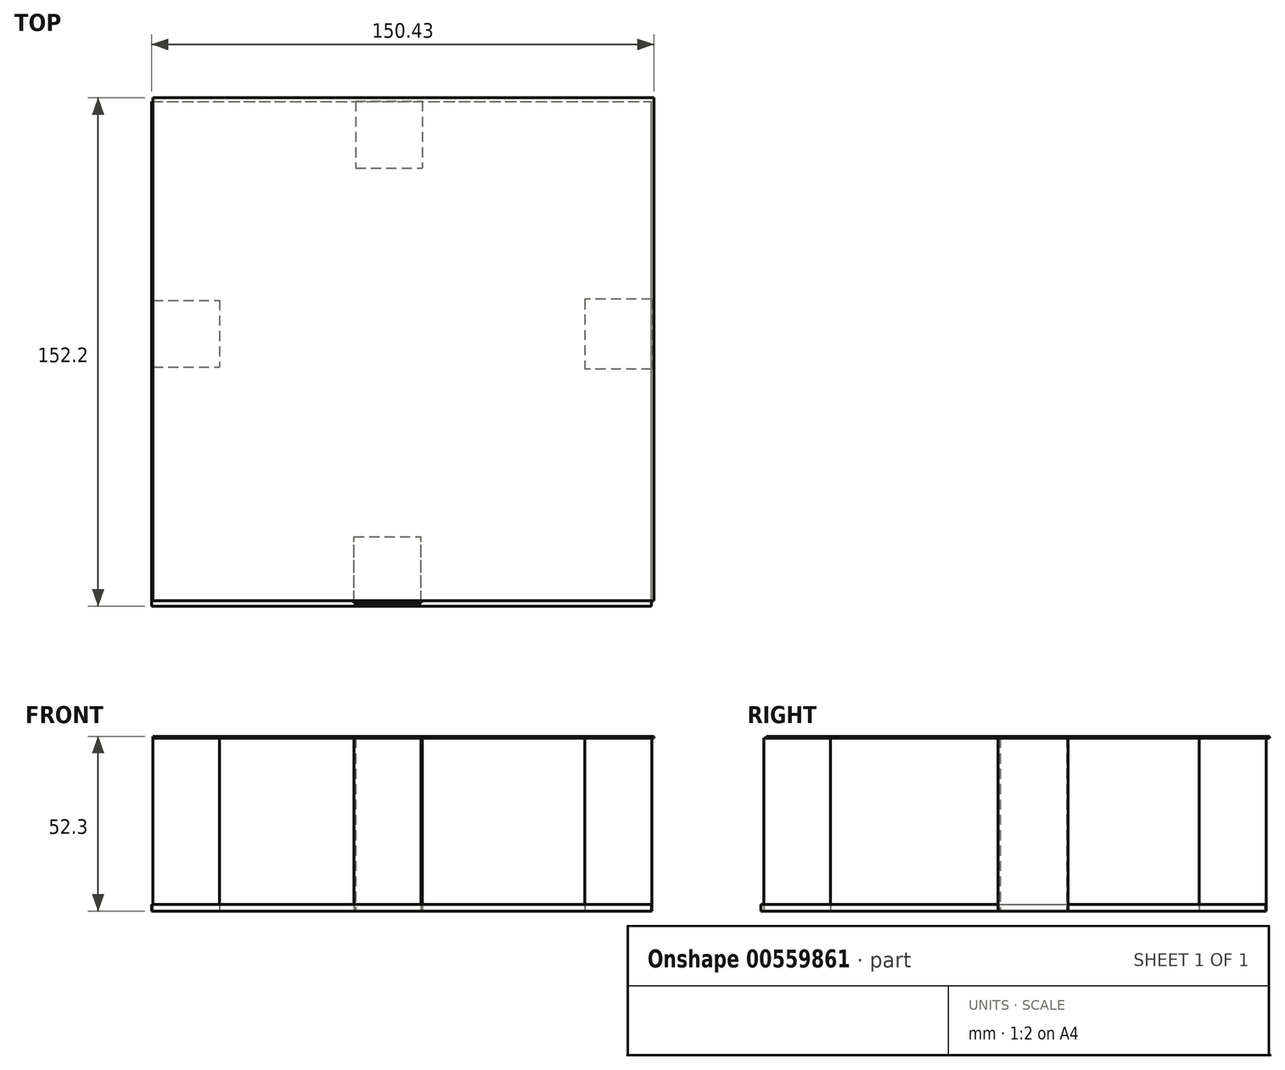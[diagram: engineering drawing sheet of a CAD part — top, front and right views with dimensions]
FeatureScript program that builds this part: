
annotation { "Feature Type Name" : "Feature", "Feature Type Description" : "" }
export const myFeature = defineFeature(function(context is Context, id is Id, definition is map)
    precondition{}
    {
        {
            var Q0;
            Q0=qCreatedBy(makeId("Top.planeOp"),FACE);
            var sketch = newSketch(context, id + "F0", { "sketchPlane" : qUnion([Q0])});
            skLineSegment(sketch, "E0.bottom", {"start": v(-89.23, 70.4) * mm, "end": v(60.77, 70.4) * mm});
            skLineSegment(sketch, "E0.top", {"start": v(-89.23, -79.6) * mm, "end": v(60.77, -79.6) * mm});
            skLineSegment(sketch, "E0.left", {"start": v(-89.23, 70.4) * mm, "end": v(-89.23, -79.6) * mm});
            skLineSegment(sketch, "E0.right", {"start": v(60.77, 70.4) * mm, "end": v(60.77, -79.6) * mm});
            skSolve(sketch);
        }
        {
            var Q0;
            Q0=makeQuery(id+"F0.imprint","IMPRINT",FACE,{"disambiguationData":[TD([[makeQuery(id+"F0.imprint","IMPRINT",EDGE,{"derivedFrom":sQuery(id+"F0.wireOp",EDGE,"E0.bottom")}),-1.0]])]});
            var sketch = newSketch(context, id + "F1", { "sketchPlane" : qUnion([Q0])});
            skLineSegment(sketch, "E1.bottom", {"start": v(-27.82, 70.37) * mm, "end": v(-7.82, 70.37) * mm});
            skLineSegment(sketch, "E1.top", {"start": v(-27.82, 50.37) * mm, "end": v(-7.82, 50.37) * mm});
            skLineSegment(sketch, "E1.left", {"start": v(-27.82, 70.37) * mm, "end": v(-27.82, 50.37) * mm});
            skLineSegment(sketch, "E1.right", {"start": v(-7.82, 70.37) * mm, "end": v(-7.82, 50.37) * mm});
            skLineSegment(sketch, "E2.bottom", {"start": v(-88.53, 10.76) * mm, "end": v(-68.53, 10.76) * mm});
            skLineSegment(sketch, "E2.top", {"start": v(-88.53, -9.24) * mm, "end": v(-68.53, -9.24) * mm});
            skLineSegment(sketch, "E2.left", {"start": v(-88.53, 10.76) * mm, "end": v(-88.53, -9.24) * mm});
            skLineSegment(sketch, "E2.right", {"start": v(-68.53, 10.76) * mm, "end": v(-68.53, -9.24) * mm});
            skLineSegment(sketch, "E3.bottom", {"start": v(-28.32, -80) * mm, "end": v(-8.32, -80) * mm});
            skLineSegment(sketch, "E3.top", {"start": v(-28.32, -60) * mm, "end": v(-8.32, -60) * mm});
            skLineSegment(sketch, "E3.left", {"start": v(-28.32, -80) * mm, "end": v(-28.32, -60) * mm});
            skLineSegment(sketch, "E3.right", {"start": v(-8.32, -80) * mm, "end": v(-8.32, -60) * mm});
            skLineSegment(sketch, "E4.bottom", {"start": v(60.77, 11.1) * mm, "end": v(40.77, 11.1) * mm});
            skLineSegment(sketch, "E4.top", {"start": v(60.77, -9.8) * mm, "end": v(40.77, -9.8) * mm});
            skLineSegment(sketch, "E4.left", {"start": v(60.77, 11.1) * mm, "end": v(60.77, -9.8) * mm});
            skLineSegment(sketch, "E4.right", {"start": v(40.77, 11.1) * mm, "end": v(40.77, -9.8) * mm});
            skSolve(sketch);
        }
        {
            var Q0;
            Q0 = qSketchRegion(id + "F1", true);
            extrude(context, id + "F2", {"entities" : qUnion([Q0]), "depth" : 51.8 * mm, "offsetDistance" : 25 * mm});
        }
        {
            var Q0;
            Q0=makeQuery(id+"F2.opExtrude","CAP_FACE",FACE,{"disambiguationData":[OSD([sQuery(id+"F1.wireOp",EDGE,"E2.bottom"),sQuery(id+"F1.wireOp",EDGE,"E2.top"),sQuery(id+"F1.wireOp",EDGE,"E2.left"),sQuery(id+"F1.wireOp",EDGE,"E2.right")])],"isStart":false});
            var sketch = newSketch(context, id + "F3", { "sketchPlane" : qUnion([Q0])});
            skLineSegment(sketch, "E5.bottom", {"start": v(-88.53, -79.19) * mm, "end": v(61.5, -79.19) * mm});
            skLineSegment(sketch, "E5.top", {"start": v(-88.53, 71.4) * mm, "end": v(61.5, 71.4) * mm});
            skLineSegment(sketch, "E5.left", {"start": v(-88.53, -79.19) * mm, "end": v(-88.53, 71.4) * mm});
            skLineSegment(sketch, "E5.right", {"start": v(61.5, -79.19) * mm, "end": v(61.5, 71.4) * mm});
            skSolve(sketch);
        }
        {
            var Q0;
            Q0 = qSketchRegion(id + "F3", true);
            extrude(context, id + "F4", {"entities" : qUnion([Q0]), "depth" : 0.5 * mm, "offsetDistance" : 25 * mm});
        }
        {
            var Q0;
            Q0=makeQuery(id+"F0.imprint","IMPRINT",FACE,{"disambiguationData":[TD([[makeQuery(id+"F0.imprint","IMPRINT",EDGE,{"derivedFrom":sQuery(id+"F0.wireOp",EDGE,"E0.bottom")}),-1.0]])]});
            var sketch = newSketch(context, id + "F5", { "sketchPlane" : qUnion([Q0])});
            skLineSegment(sketch, "E6.bottom", {"start": v(-88.93, -80.8) * mm, "end": v(60.65, -80.8) * mm});
            skLineSegment(sketch, "E6.top", {"start": v(-88.93, 70.24) * mm, "end": v(60.65, 70.24) * mm});
            skLineSegment(sketch, "E6.left", {"start": v(-88.93, -80.8) * mm, "end": v(-88.93, 70.24) * mm});
            skLineSegment(sketch, "E6.right", {"start": v(60.65, -80.8) * mm, "end": v(60.65, 70.24) * mm});
            skSolve(sketch);
        }
        {
            var Q0;
            Q0 = qSketchRegion(id + "F5", true);
            extrude(context, id + "F6", {"entities" : qUnion([Q0]), "depth" : 2 * mm, "offsetDistance" : 25 * mm});
        }
    });
